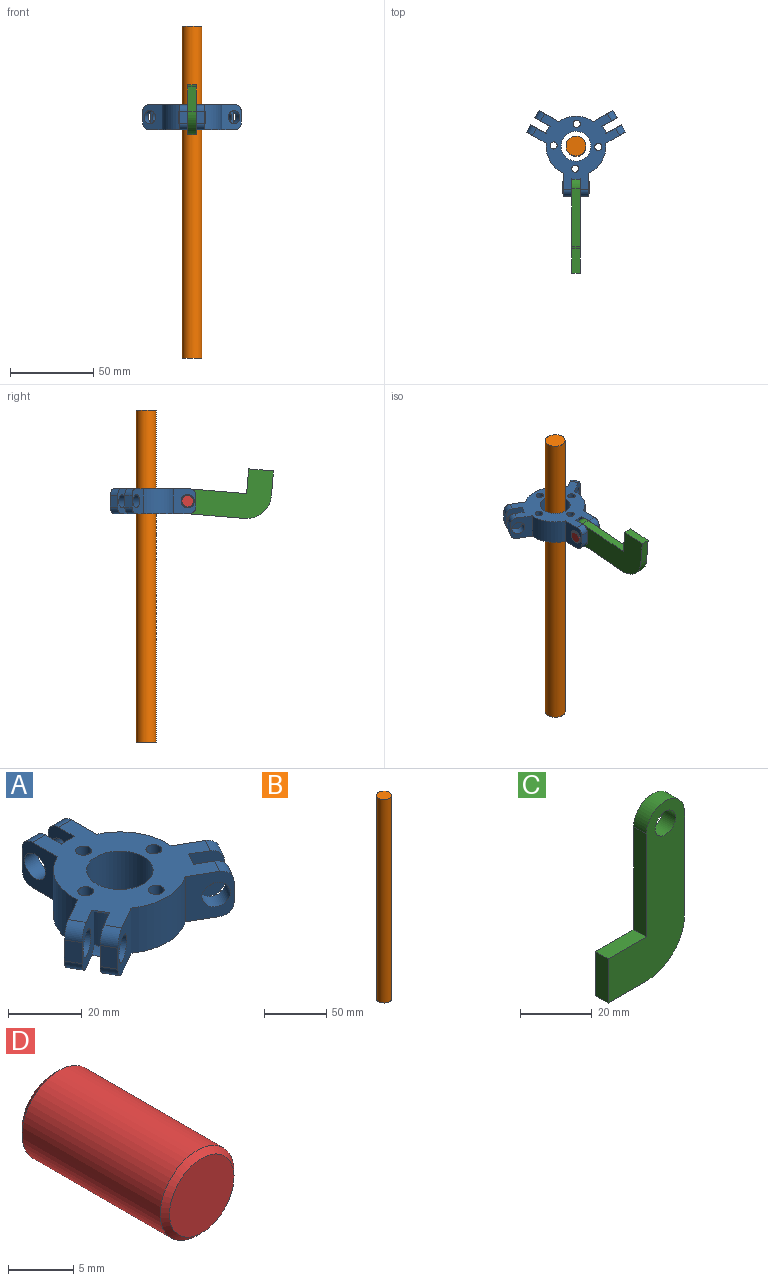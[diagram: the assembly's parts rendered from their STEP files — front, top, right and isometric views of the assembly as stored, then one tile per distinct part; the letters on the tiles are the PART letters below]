
ASSEMBLY  parts=4 mates=3
PART A: 55 faces, bbox 59.5x51.5x15 mm
  f0: plane 7x4.33mm, normal (0.87,-0.5,0), area 35mm2, adj f1,f5,f6,f8
  f1: plane 15x10.54mm, normal (-0.5,-0.87,0), area 121.5mm2, adj f0,f6,f8,f14,f22,f23,f24,f42
  f2: plane 15x10.54mm, normal (0.5,0.87,0), area 121.5mm2, adj f3,f7,f9,f10,f14,f22,f23,f42
  f3: plane 7x4.33mm, normal (0.87,-0.5,0), area 35mm2, adj f2,f4,f7,f9
  f4: plane 15x11.81mm, normal (-0.5,-0.87,0), area 147.4mm2, adj f3,f7,f9,f10,f11,f42,f43
  f5: plane 15x11.81mm, normal (0.5,0.87,0), area 147.4mm2, adj f0,f6,f8,f16,f24,f42,f43
  f6: cylinder r=4mm len=6.33mm, axis (-0.5,-0.87,0), area 31.4mm2, adj f0,f1,f5,f42
  f7: cylinder r=4mm len=6.33mm, axis (-0.5,-0.87,0), area 31.4mm2, adj f2,f3,f4,f42
  f8: cylinder r=4mm len=6.33mm, axis (0.5,0.87,0), area 31.4mm2, adj f0,f1,f5,f43
  f9: cylinder r=4mm len=6.33mm, axis (0.5,0.87,0), area 31.4mm2, adj f2,f3,f4,f43
  f10: cylinder r=4mm len=9.43mm, axis (0.5,0.87,0), area 125.7mm2, adj f2,f4
  f11: cylinder r=18mm len=20.84mm, axis (0,0,1), area 333.4mm2, adj f4,f34,f42,f43
  f12: cylinder r=18mm len=18.05mm, axis (0,0,1), area 333.4mm2, adj f37,f42,f43,f44
  f13: cylinder r=18mm len=10.91mm, axis (0,0,1), area 54.7mm2, adj f20,f21,f27,f28
  f14: cylinder r=18mm len=10.91mm, axis (0,0,1), area 54.7mm2, adj f1,f2,f22,f23
  f15: cylinder r=4mm len=6.33mm, axis (0.5,-0.87,0), area 31.4mm2, adj f28,f36,f37,f43
  f16: cylinder r=18mm len=18.05mm, axis (0,0,1), area 333.4mm2, adj f5,f42,f43,f52
  f17: plane 15x12.17mm, normal (-1,0,0), area 121.5mm2, adj f18,f19,f26,f42,f43,f47,f49,f50
  f18: cylinder r=9.01mm len=5mm, axis (-1,0,0), area 14mm2, adj f17,f25,f26,f42
  f19: cylinder r=9.01mm len=5mm, axis (-1,0,0), area 14mm2, adj f17,f25,f26,f43
  f20: cylinder r=9.01mm len=5.42mm, axis (0.5,-0.87,0), area 14mm2, adj f13,f27,f28,f42
  f21: cylinder r=9.01mm len=5.42mm, axis (0.5,-0.87,0), area 14mm2, adj f13,f27,f28,f43
  f22: cylinder r=9.01mm len=5.42mm, axis (0.5,0.87,0), area 14mm2, adj f1,f2,f14,f42
  f23: cylinder r=9.01mm len=5.42mm, axis (0.5,0.87,0), area 14mm2, adj f1,f2,f14,f43
  f24: cylinder r=4mm len=9.43mm, axis (0.5,0.87,0), area 125.7mm2, adj f1,f5
  f25: plane 15x12.17mm, normal (1,0,0), area 121.5mm2, adj f18,f19,f26,f42,f43,f46,f48,f51
  f26: cylinder r=18mm len=10.91mm, axis (0,0,1), area 54.7mm2, adj f17,f18,f19,f25
  f27: plane 15x10.54mm, normal (-0.5,0.87,0), area 121.5mm2, adj f13,f20,f21,f29,f31,f33,f35,f42
  f28: plane 15x10.54mm, normal (0.5,-0.87,0), area 121.5mm2, adj f13,f15,f20,f21,f30,f32,f36,f42
  f29: cylinder r=4mm len=6.33mm, axis (0.5,-0.87,0), area 31.4mm2, adj f27,f34,f35,f43
  f30: cylinder r=4mm len=6.33mm, axis (-0.5,0.87,0), area 31.4mm2, adj f28,f36,f37,f42
  f31: cylinder r=4mm len=6.33mm, axis (-0.5,0.87,0), area 31.4mm2, adj f27,f34,f35,f42
  f32: cylinder r=4mm len=9.43mm, axis (0.5,-0.87,0), area 125.7mm2, adj f28,f37
  f33: cylinder r=4mm len=9.43mm, axis (0.5,-0.87,0), area 125.7mm2, adj f27,f34
  f34: plane 15x11.81mm, normal (0.5,-0.87,0), area 147.4mm2, adj f11,f29,f31,f33,f35,f42,f43
  f35: plane 7x4.33mm, normal (-0.87,-0.5,0), area 35mm2, adj f27,f29,f31,f34
  f36: plane 7x4.33mm, normal (-0.87,-0.5,0), area 35mm2, adj f15,f28,f30,f37
  f37: plane 15x11.81mm, normal (-0.5,0.87,0), area 147.4mm2, adj f12,f15,f30,f32,f36,f42,f43
  f38: cylinder r=2.15mm len=15mm, axis (0,0,1), area 202.6mm2, adj f42,f43
  f39: cylinder r=2.15mm len=15mm, axis (0,0,1), area 202.6mm2, adj f42,f43
  f40: cylinder r=2.15mm len=15mm, axis (0,0,1), area 202.6mm2, adj f42,f43
  f41: cylinder r=2.15mm len=15mm, axis (0,0,1), area 202.6mm2, adj f42,f43
  f42: plane 52.53x45.5mm, normal (0,0,-1), area 999.4mm2, adj f1,f2,f4,f5,f6,f7,f11,f12
  f43: plane 52.53x45.5mm, normal (0,0,1), area 999.4mm2, adj f1,f2,f4,f5,f8,f9,f11,f12
  f44: plane 15x13.64mm, normal (-1,0,0), area 147.4mm2, adj f12,f42,f43,f46,f48,f51,f54
  f45: cylinder r=9mm len=18mm, axis (0,0,1), area 848.2mm2, adj f42,f43
  f46: cylinder r=4mm len=5mm, axis (1,0,0), area 31.4mm2, adj f25,f42,f44,f51
  f47: cylinder r=4mm len=5mm, axis (1,0,0), area 31.4mm2, adj f17,f42,f50,f52
  f48: cylinder r=4mm len=5mm, axis (-1,0,0), area 31.4mm2, adj f25,f43,f44,f51
  f49: cylinder r=4mm len=5mm, axis (-1,0,0), area 31.4mm2, adj f17,f43,f50,f52
  f50: plane 7x5mm, normal (0,1,0), area 35mm2, adj f17,f47,f49,f52
  f51: plane 7x5mm, normal (0,1,0), area 35mm2, adj f25,f44,f46,f48
  f52: plane 15x13.64mm, normal (1,0,0), area 147.4mm2, adj f16,f42,f43,f47,f49,f50,f53
  f53: cylinder r=4mm len=8mm, axis (-1,0,0), area 125.7mm2, adj f17,f52
  f54: cylinder r=4mm len=8mm, axis (-1,0,0), area 125.7mm2, adj f25,f44
PART B: 3 faces, bbox 12x12x200 mm
  f0: cylinder r=6mm len=200mm, axis (0,0,-1), area 7539.8mm2, adj f1,f2
  f1: plane 12x12mm, normal (0,0,1), area 113.1mm2, adj f0
  f2: plane 12x12mm, normal (0,0,-1), area 113.1mm2, adj f0
PART C: 10 faces, bbox 30x5x57.5 mm
  f0: plane 35x5mm, normal (1,0,0), area 175mm2, adj f1,f7,f8,f9
  f1: cylinder r=7.5mm len=15mm, axis (0,1,0), area 117.8mm2, adj f0,f2,f7,f8
  f2: plane 35x5mm, normal (-1,0,0), area 175mm2, adj f1,f3,f7,f8
  f3: plane 15x5mm, normal (0,0,1), area 75mm2, adj f2,f4,f7,f8
  f4: plane 15x5mm, normal (-1,0,0), area 75mm2, adj f3,f5,f7,f8
  f5: plane 15x5mm, normal (0,0,-1), area 75mm2, adj f4,f7,f8,f9
  f6: cylinder r=4mm len=8mm, axis (0,1,0), area 125.7mm2, adj f7,f8
  f7: plane 57.5x30mm, normal (0,-1,0), area 964.8mm2, adj f0,f1,f2,f3,f4,f5,f6,f9
  f8: plane 57.5x30mm, normal (0,1,0), area 964.8mm2, adj f0,f1,f2,f3,f4,f5,f6,f9
  f9: cylinder r=15mm len=15mm, axis (0,1,0), area 117.8mm2, adj f0,f5,f7,f8
PART D: 5 faces, bbox 8x16x8 mm
  f0: cylinder r=4mm len=15mm, axis (0,1,0), area 377mm2, adj f3,f4
  f1: plane 7x7mm, normal (0,-1,0), area 38.5mm2, adj f3
  f2: plane 7x7mm, normal (0,1,0), area 38.5mm2, adj f4
  f3: cone r=3.5mm half-angle=45deg, axis (0,1,0), area 16.7mm2, adj f0,f1
  f4: cone r=4mm half-angle=45deg, axis (0,-1,0), area 16.7mm2, adj f0,f2
PLACE A rot(axis=(1,0,0),180deg) t=(0,0,152.55)mm
PLACE B at identity
PLACE C rot(axis=(-0.56,0.56,0.61),117.3deg) t=(-2.5,-25.63,152.53)mm
PLACE D rot(axis=(0,0,1),90deg) t=(-8,-25,145.05)mm
MATE revolute C.f1 <-> D.f0  axis (-1,0,0) through (0,-25,145.05)mm
MATE revolute D.f0 <-> A.f18  axis (1,0,0) through (7.5,-25,145.05)mm
MATE slider A.f45 <-> B.f0  axis (0,0,-1) through (0,0,137.55)mm
